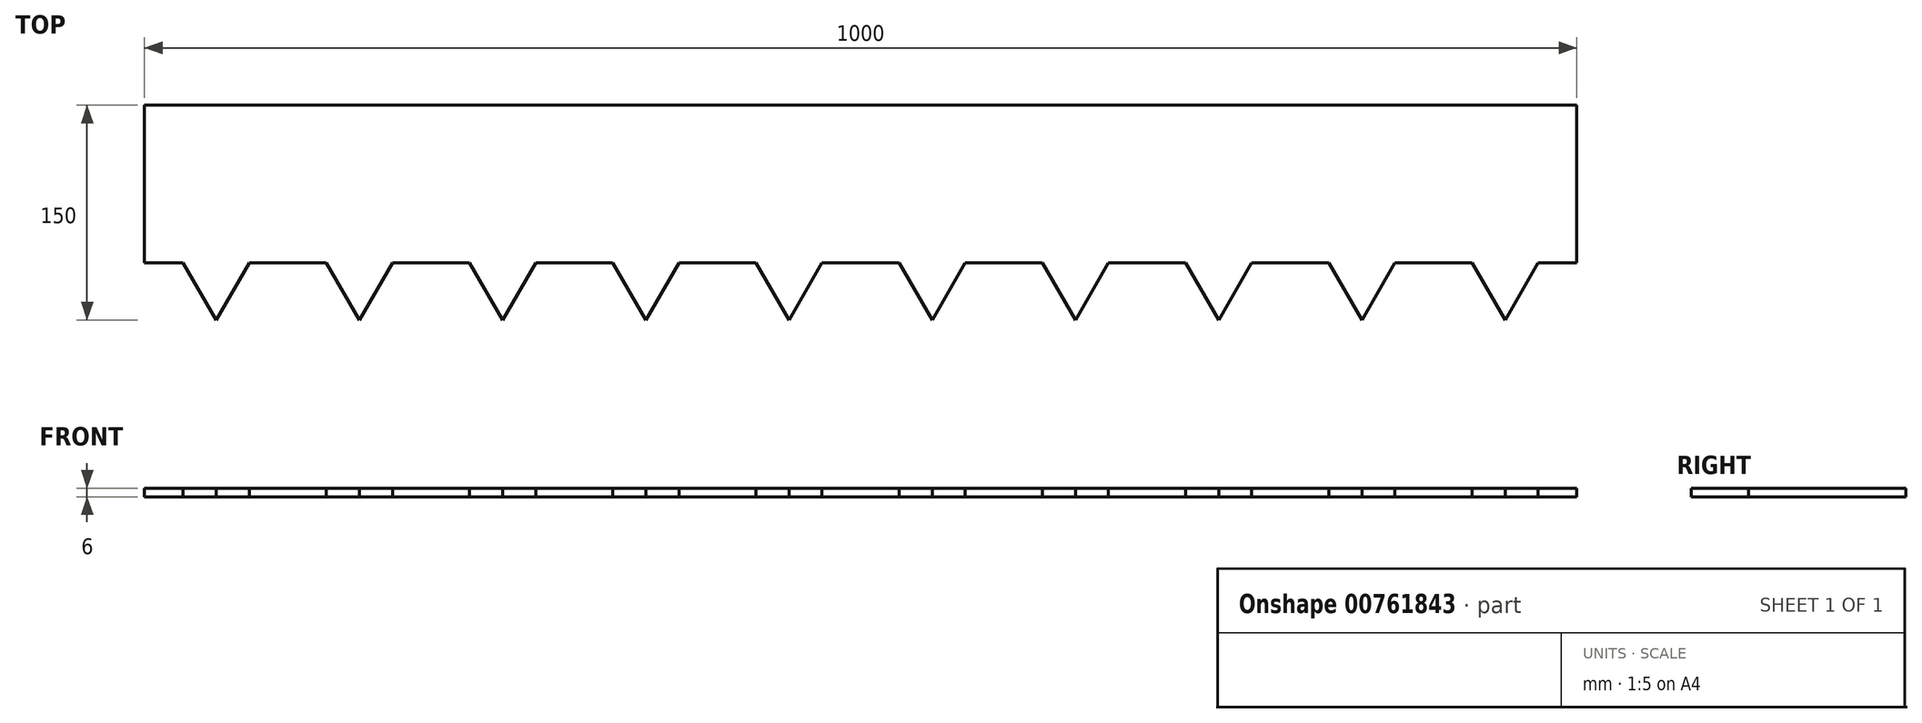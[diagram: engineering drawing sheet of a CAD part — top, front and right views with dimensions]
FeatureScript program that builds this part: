
annotation { "Feature Type Name" : "Feature", "Feature Type Description" : "" }
export const myFeature = defineFeature(function(context is Context, id is Id, definition is map)
    precondition{}
    {
        {
            var Q0;
            Q0=qCreatedBy(makeId("Top.planeOp"),FACE);
            var sketch = newSketch(context, id + "F0", { "sketchPlane" : qUnion([Q0])});
            skLineSegment(sketch, "E0", {"start": v(0, 0) * mm, "end": v(1000, 0) * mm});
            skLineSegment(sketch, "E1", {"start": v(1000, 0) * mm, "end": v(1000, -110) * mm});
            skLineSegment(sketch, "E2", {"start": v(1000, -110) * mm, "end": v(0, -110) * mm});
            skLineSegment(sketch, "E3", {"start": v(0, -110) * mm, "end": v(0, 0) * mm});
            skLineSegment(sketch, "E4", {"start": v(50, -34.04) * mm, "end": v(50, -150) * mm, "construction": true});
            skLineSegment(sketch, "E5", {"start": v(50, -150) * mm, "end": v(104.61, -55.4) * mm});
            skLineSegment(sketch, "E6.MirrorCS", {"start": v(50, -150) * mm, "end": v(-4.61, -55.4) * mm});
            skLineSegment(sketch, "E7.1.0.0", {"start": v(150, -150) * mm, "end": v(95.39, -55.4) * mm});
            skLineSegment(sketch, "E7.1.0.1", {"start": v(150, -150) * mm, "end": v(204.61, -55.4) * mm});
            skLineSegment(sketch, "E7.2.0.0", {"start": v(250, -150) * mm, "end": v(195.39, -55.4) * mm});
            skLineSegment(sketch, "E7.2.0.1", {"start": v(250, -150) * mm, "end": v(304.61, -55.4) * mm});
            skLineSegment(sketch, "E7.3.0.0", {"start": v(350, -150) * mm, "end": v(295.39, -55.4) * mm});
            skLineSegment(sketch, "E7.3.0.1", {"start": v(350, -150) * mm, "end": v(404.61, -55.4) * mm});
            skLineSegment(sketch, "E7.4.0.0", {"start": v(450, -150) * mm, "end": v(395.39, -55.4) * mm});
            skLineSegment(sketch, "E7.4.0.1", {"start": v(450, -150) * mm, "end": v(504.61, -55.4) * mm});
            skLineSegment(sketch, "E7.5.0.0", {"start": v(550, -150) * mm, "end": v(495.39, -55.4) * mm});
            skLineSegment(sketch, "E7.5.0.1", {"start": v(550, -150) * mm, "end": v(604.61, -55.4) * mm});
            skLineSegment(sketch, "E7.6.0.0", {"start": v(650, -150) * mm, "end": v(595.39, -55.4) * mm});
            skLineSegment(sketch, "E7.6.0.1", {"start": v(650, -150) * mm, "end": v(704.61, -55.4) * mm});
            skLineSegment(sketch, "E7.7.0.0", {"start": v(750, -150) * mm, "end": v(695.39, -55.4) * mm});
            skLineSegment(sketch, "E7.7.0.1", {"start": v(750, -150) * mm, "end": v(804.61, -55.4) * mm});
            skLineSegment(sketch, "E7.8.0.0", {"start": v(850, -150) * mm, "end": v(795.39, -55.4) * mm});
            skLineSegment(sketch, "E7.8.0.1", {"start": v(850, -150) * mm, "end": v(904.61, -55.4) * mm});
            skLineSegment(sketch, "E7.9.0.0", {"start": v(950, -150) * mm, "end": v(895.39, -55.4) * mm});
            skLineSegment(sketch, "E7.9.0.1", {"start": v(950, -150) * mm, "end": v(1004.61, -55.4) * mm});
            skLineSegment(sketch, "E7.direction1", {"start": v(50, -150) * mm, "end": v(150, -150) * mm, "construction": true});
            skSolve(sketch);
        }
        {
            var Q0;
            Q0 = qSketchRegion(id + "F0", true);
            extrude(context, id + "F1", {"entities" : qUnion([Q0]), "depth" : 6 * mm, "offsetDistance" : 25 * mm});
        }
    });
